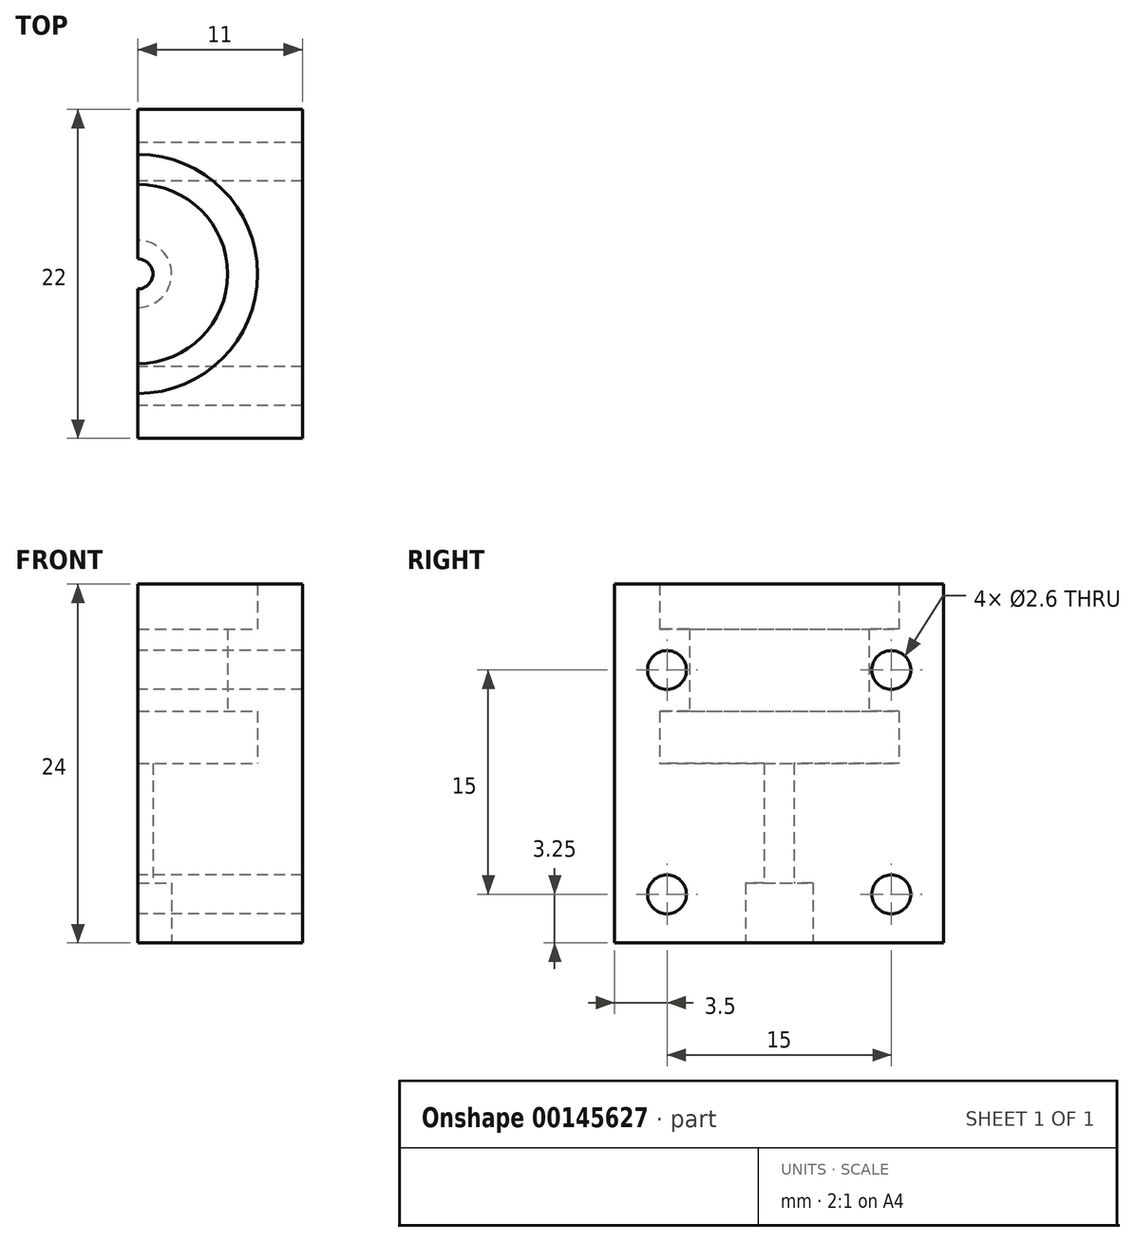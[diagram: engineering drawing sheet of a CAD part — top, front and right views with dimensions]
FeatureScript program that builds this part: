
annotation { "Feature Type Name" : "Feature", "Feature Type Description" : "" }
export const myFeature = defineFeature(function(context is Context, id is Id, definition is map)
    precondition{}
    {
        {
            assignVariable(context, id + "F0", {"name" : "height", "anyValue" : 24});
        }
        {
            var Q0;
            Q0=qCreatedBy(makeId("Top.planeOp"),FACE);
            var sketch = newSketch(context, id + "F1", { "sketchPlane" : qUnion([Q0])});
            skLineSegment(sketch, "E0.left", {"start": v(-11, 11) * mm, "end": v(-11, -11) * mm});
            skLineSegment(sketch, "E0.right", {"start": v(11, 11) * mm, "end": v(11, -11) * mm});
            skPoint(sketch, "E0.middle", {"position": v(0, 0) * mm});
            skCircle(sketch, "E1", {"center": v(0, 0) * mm, "radius": 8 * mm});
            skCircle(sketch, "E2", {"center": v(0, 0) * mm, "radius": 6 * mm});
            skCircle(sketch, "E3", {"center": v(0, 0) * mm, "radius": 2.25 * mm});
            skCircle(sketch, "E4", {"center": v(0, 0) * mm, "radius": 1 * mm});
            skLineSegment(sketch, "E5", {"start": v(0, 11) * mm, "end": v(0, -11) * mm});
            skLineSegment(sketch, "E6", {"start": v(0, -11) * mm, "end": v(11, -11) * mm});
            skLineSegment(sketch, "E7", {"start": v(-11, -11) * mm, "end": v(0, -11) * mm});
            skLineSegment(sketch, "E8", {"start": v(0, 11) * mm, "end": v(11, 11) * mm});
            skLineSegment(sketch, "E9", {"start": v(-11, 11) * mm, "end": v(0, 11) * mm});
            skSolve(sketch);
        }
        {
            var Q0;
            {var subQ6=sQuery(id+"F1.wireOp",EDGE,"E0.right");Q0=makeQuery(id+"F1.imprint","IMPRINT",FACE,{"disambiguationData":[TD([[makeQuery(id+"F1.imprint","IMPRINT",EDGE,{"derivedFrom":subQ6}),-1.0]])]});}
            extrude(context, id + "F2", {"entities" : qUnion([Q0]), "depth" : (getVariable(context, 'height')) * mm});
        }
        {
            var Q0;
            {var subQ0=sQuery(id+"F1.wireOp",EDGE,"E5");var subQ1=sQuery(id+"F1.wireOp",EDGE,"E1");var subQ2=makeQuery(id+"F1.imprint","INTERSECT",VERTEX,{"disambiguationData":[OD(0.0)],"derivedFrom":[subQ1,subQ0]});Q0=makeQuery(id+"F1.imprint","IMPRINT",FACE,{"disambiguationData":[TD([[makeQuery(id+"F1.imprint","IMPRINT",EDGE,{"disambiguationData":[TD([[subQ2,1.0]])],"derivedFrom":subQ1}),1.0]])]});}
            extrude(context, id + "F3", {"entities" : qUnion([Q0]), "operationType" : NewBodyOperationType.ADD, "depth" : (getVariable(context, 'height') - 3) * mm});
        }
        {
            var Q0;
            {var subQ0=sQuery(id+"F1.wireOp",EDGE,"E5");var subQ1=sQuery(id+"F1.wireOp",EDGE,"E1");var subQ2=makeQuery(id+"F1.imprint","INTERSECT",VERTEX,{"disambiguationData":[OD(0.0)],"derivedFrom":[subQ1,subQ0]});Q0=makeQuery(id+"F1.imprint","IMPRINT",FACE,{"disambiguationData":[TD([[makeQuery(id+"F1.imprint","IMPRINT",EDGE,{"disambiguationData":[TD([[subQ2,1.0]])],"derivedFrom":subQ1}),1.0]])]});}
            var Q1;
            {var subQ0=sQuery(id+"F1.wireOp",EDGE,"E5");var subQ1=sQuery(id+"F1.wireOp",EDGE,"E1");var subQ2=makeQuery(id+"F1.imprint","INTERSECT",VERTEX,{"disambiguationData":[OD(0.0)],"derivedFrom":[subQ1,subQ0]});Q1=makeQuery(id+"F1.imprint","IMPRINT",FACE,{"disambiguationData":[TD([[makeQuery(id+"F1.imprint","IMPRINT",EDGE,{"disambiguationData":[TD([[subQ2,-1.0]])],"derivedFrom":subQ1}),1.0]])]});}
            extrude(context, id + "F4", {"entities" : qUnion([Q0, Q1]), "operationType" : NewBodyOperationType.REMOVE, "depth" : (getVariable(context, 'height') - 3 - 5.5) * mm});
        }
        {
            var Q0;
            {var subQ0=sQuery(id+"F1.wireOp",EDGE,"E5");var subQ1=sQuery(id+"F1.wireOp",EDGE,"E1");var subQ2=makeQuery(id+"F1.imprint","INTERSECT",VERTEX,{"disambiguationData":[OD(0.0)],"derivedFrom":[subQ1,subQ0]});Q0=makeQuery(id+"F1.imprint","IMPRINT",FACE,{"disambiguationData":[TD([[makeQuery(id+"F1.imprint","IMPRINT",EDGE,{"disambiguationData":[TD([[subQ2,1.0]])],"derivedFrom":subQ1}),1.0]])]});}
            var Q1;
            {var subQ0=sQuery(id+"F1.wireOp",EDGE,"E5");var subQ1=sQuery(id+"F1.wireOp",EDGE,"E2");var subQ2=makeQuery(id+"F1.imprint","INTERSECT",VERTEX,{"disambiguationData":[OD(0.0)],"derivedFrom":[subQ1,subQ0]});Q1=makeQuery(id+"F1.imprint","IMPRINT",FACE,{"disambiguationData":[TD([[makeQuery(id+"F1.imprint","IMPRINT",EDGE,{"disambiguationData":[TD([[subQ2,1.0]])],"derivedFrom":subQ1}),1.0]])]});}
            var Q2;
            {var subQ0=sQuery(id+"F1.wireOp",EDGE,"E5");var subQ1=sQuery(id+"F1.wireOp",EDGE,"E3");var subQ2=makeQuery(id+"F1.imprint","INTERSECT",VERTEX,{"disambiguationData":[OD(0.0)],"derivedFrom":[subQ1,subQ0]});Q2=makeQuery(id+"F1.imprint","IMPRINT",FACE,{"disambiguationData":[TD([[makeQuery(id+"F1.imprint","IMPRINT",EDGE,{"disambiguationData":[TD([[subQ2,1.0]])],"derivedFrom":subQ1}),1.0]])]});}
            extrude(context, id + "F5", {"entities" : qUnion([Q0, Q1, Q2]), "operationType" : NewBodyOperationType.ADD, "depth" : (getVariable(context, 'height') - 3 - 5.5 - 3.5) * mm});
        }
        {
            var Q0;
            {var subQ0=sQuery(id+"F1.wireOp",EDGE,"E5");var subQ1=sQuery(id+"F1.wireOp",EDGE,"E3");var subQ2=makeQuery(id+"F1.imprint","INTERSECT",VERTEX,{"disambiguationData":[OD(0.0)],"derivedFrom":[subQ1,subQ0]});Q0=makeQuery(id+"F1.imprint","IMPRINT",FACE,{"disambiguationData":[TD([[makeQuery(id+"F1.imprint","IMPRINT",EDGE,{"disambiguationData":[TD([[subQ2,1.0]])],"derivedFrom":subQ1}),1.0]])]});}
            var Q1;
            {var subQ0=sQuery(id+"F1.wireOp",EDGE,"E5");var subQ1=sQuery(id+"F1.wireOp",EDGE,"E3");var subQ2=makeQuery(id+"F1.imprint","INTERSECT",VERTEX,{"disambiguationData":[OD(0.0)],"derivedFrom":[subQ1,subQ0]});Q1=makeQuery(id+"F1.imprint","IMPRINT",FACE,{"disambiguationData":[TD([[makeQuery(id+"F1.imprint","IMPRINT",EDGE,{"disambiguationData":[TD([[subQ2,-1.0]])],"derivedFrom":subQ1}),1.0]])]});}
            extrude(context, id + "F6", {"entities" : qUnion([Q0, Q1]), "operationType" : NewBodyOperationType.REMOVE, "depth" : 4 * mm});
        }
        {
            var Q0;
            {var subQ0=sQuery(id+"F1.wireOp",EDGE,"E5");var subQ1=makeQuery(id+"F1.imprint","INTERSECT",VERTEX,{"disambiguationData":[OD(0.0)],"derivedFrom":[sQuery(id+"F1.wireOp",EDGE,"E3"),subQ0]});var subQ2=makeQuery(id+"F1.imprint","INTERSECT",VERTEX,{"disambiguationData":[OD(0.0)],"derivedFrom":[sQuery(id+"F1.wireOp",EDGE,"E2"),subQ0]});var subQ3=makeQuery(id+"F1.imprint","INTERSECT",VERTEX,{"disambiguationData":[OD(0.0)],"derivedFrom":[sQuery(id+"F1.wireOp",EDGE,"E1"),subQ0]});var subQ4=makeQuery(id+"F1.imprint","IMPRINT",EDGE,{"disambiguationData":[TD([[subQ3,-1.0]])],"derivedFrom":subQ0});Q0=makeQuery(id+"F5.boolean.opBoolean","MERGE",FACE,{"derivedFrom":[makeQuery(id+"F3.boolean.opBoolean","MERGE",FACE,{"derivedFrom":[makeQuery(id+"F2.opExtrude","SWEPT_FACE",FACE,{"disambiguationData":[OSD([subQ0]),TDD([makeQuery(id+"F1.imprint","IMPRINT",EDGE,{"disambiguationData":[TD([[makeQuery(id+"F1.imprint","INTERSECT",VERTEX,{"derivedFrom":[sQuery(id+"F1.wireOp",EDGE,"E0.bottom"),subQ0]}),-1.0]])],"derivedFrom":subQ0})])]}),makeQuery(id+"F3.opExtrude","SWEPT_FACE",FACE,{"disambiguationData":[OSD([subQ0]),TDD([subQ4])]})]}),makeQuery(id+"F5.opExtrude","SWEPT_FACE",FACE,{"disambiguationData":[OSD([subQ0]),TDD([subQ4,makeQuery(id+"F1.imprint","IMPRINT",EDGE,{"disambiguationData":[TD([[subQ2,-1.0]])],"derivedFrom":subQ0}),makeQuery(id+"F1.imprint","IMPRINT",EDGE,{"disambiguationData":[TD([[subQ1,-1.0]])],"derivedFrom":subQ0})])]})]});}
            var sketch = newSketch(context, id + "F7", { "sketchPlane" : qUnion([Q0])});
            skPoint(sketch, "E10", {"position": v(-6, 18.25) * mm});
            skPoint(sketch, "E11", {"position": v(6, 18.25) * mm});
            skLineSegment(sketch, "E12", {"start": v(-6, 18.25) * mm, "end": v(6, 18.25) * mm, "construction": true});
            skLineSegment(sketch, "E13", {"start": v(6, 18.25) * mm, "end": v(7.5, 18.25) * mm, "construction": true});
            skLineSegment(sketch, "E14", {"start": v(-6, 18.25) * mm, "end": v(-7.5, 18.25) * mm, "construction": true});
            skCircle(sketch, "E15", {"center": v(-7.5, 18.25) * mm, "radius": 1.3 * mm});
            skCircle(sketch, "E16", {"center": v(7.5, 18.25) * mm, "radius": 1.3 * mm});
            skLineSegment(sketch, "E17", {"start": v(-7.5, 18.25) * mm, "end": v(-7.5, 3.25) * mm, "construction": true});
            skLineSegment(sketch, "E18", {"start": v(7.5, 18.25) * mm, "end": v(7.5, 3.25) * mm, "construction": true});
            skCircle(sketch, "E19", {"center": v(-7.5, 3.25) * mm, "radius": 1.3 * mm});
            skCircle(sketch, "E20", {"center": v(7.5, 3.25) * mm, "radius": 1.3 * mm});
            skSolve(sketch);
        }
        {
            var Q0;
            Q0=makeQuery(id+"F7.imprint","IMPRINT",FACE,{"disambiguationData":[TD([[makeQuery(id+"F7.imprint","IMPRINT",EDGE,{"derivedFrom":sQuery(id+"F7.wireOp",EDGE,"E15")}),1.0]])]});
            var Q1;
            Q1=makeQuery(id+"F7.imprint","IMPRINT",FACE,{"disambiguationData":[TD([[makeQuery(id+"F7.imprint","IMPRINT",EDGE,{"derivedFrom":sQuery(id+"F7.wireOp",EDGE,"E16")}),1.0]])]});
            var Q2;
            Q2=makeQuery(id+"F7.imprint","IMPRINT",FACE,{"disambiguationData":[TD([[makeQuery(id+"F7.imprint","IMPRINT",EDGE,{"derivedFrom":sQuery(id+"F7.wireOp",EDGE,"E20")}),1.0]])]});
            var Q3;
            Q3=makeQuery(id+"F7.imprint","IMPRINT",FACE,{"disambiguationData":[TD([[makeQuery(id+"F7.imprint","IMPRINT",EDGE,{"derivedFrom":sQuery(id+"F7.wireOp",EDGE,"E19")}),1.0]])]});
            extrude(context, id + "F8", {"entities" : qUnion([Q0, Q1, Q2, Q3]), "operationType" : NewBodyOperationType.REMOVE, "endBound" : BoundingType.THROUGH_ALL, "oppositeDirection" : true, "depth" : 25 * mm});
        }
    });
